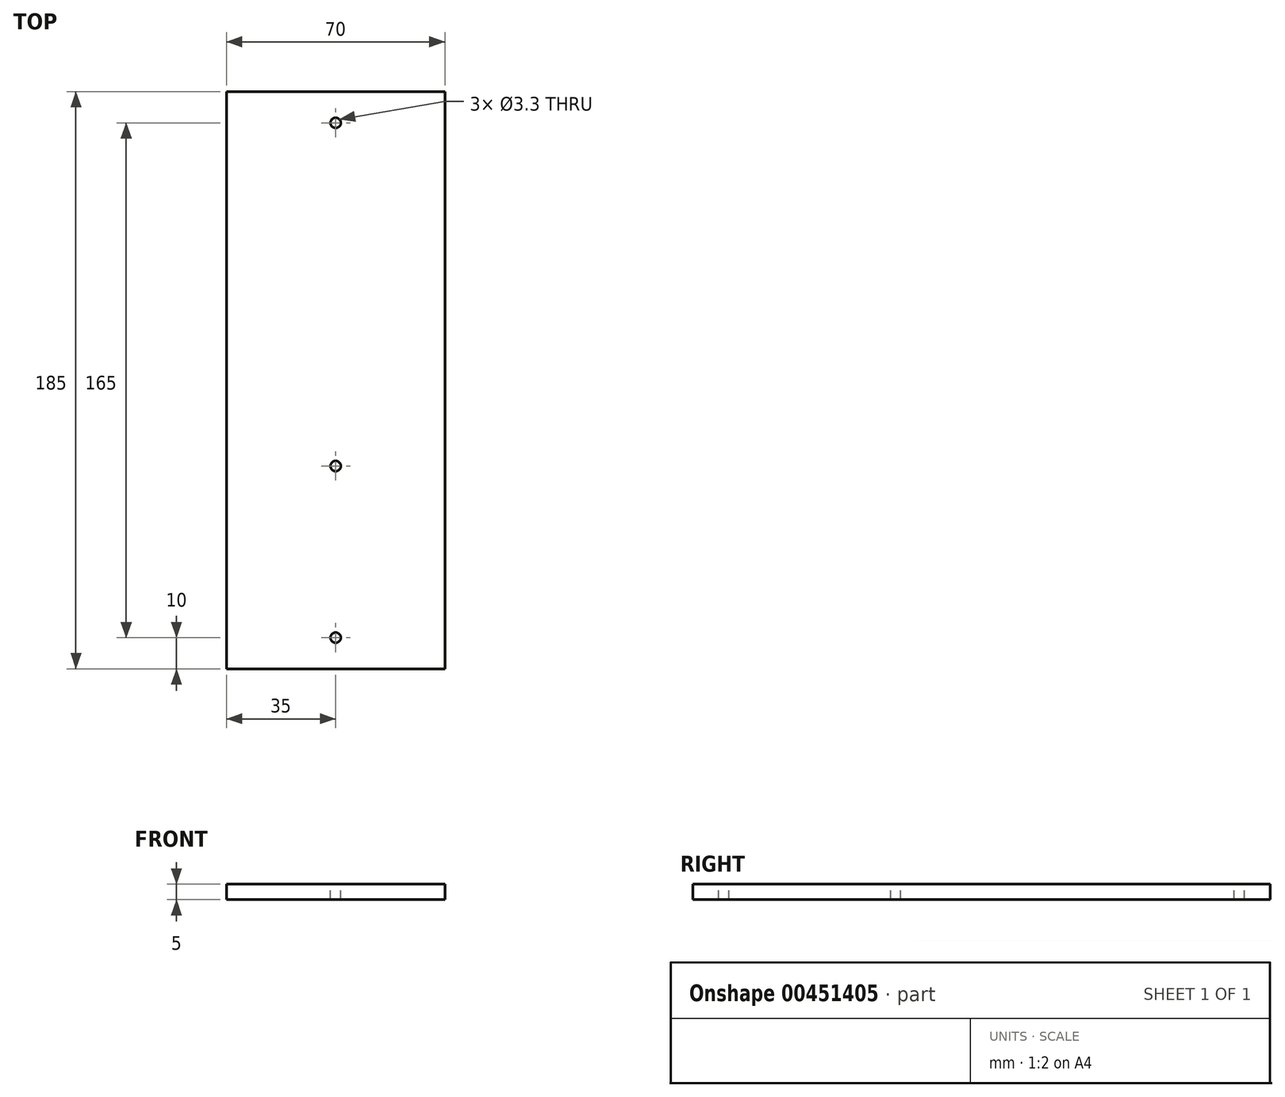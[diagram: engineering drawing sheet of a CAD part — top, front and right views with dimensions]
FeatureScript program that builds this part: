
annotation { "Feature Type Name" : "Feature", "Feature Type Description" : "" }
export const myFeature = defineFeature(function(context is Context, id is Id, definition is map)
    precondition{}
    {
        {
            var Q0;
            Q0=qCreatedBy(makeId("Top.planeOp"),FACE);
            var sketch = newSketch(context, id + "F0", { "sketchPlane" : qUnion([Q0])});
            skLineSegment(sketch, "E0.bottom", {"start": v(0, 0) * mm, "end": v(70, 0) * mm});
            skLineSegment(sketch, "E0.top", {"start": v(0, 185) * mm, "end": v(70, 185) * mm});
            skLineSegment(sketch, "E0.left", {"start": v(0, 0) * mm, "end": v(0, 185) * mm});
            skLineSegment(sketch, "E0.right", {"start": v(70, 0) * mm, "end": v(70, 185) * mm});
            skSolve(sketch);
        }
        {
            var Q0;
            Q0 = qSketchRegion(id + "F0", true);
            extrude(context, id + "F1", {"entities" : qUnion([Q0]), "depth" : 5 * mm});
        }
        {
            var Q0;
            Q0=makeQuery(id+"F1.opExtrude","CAP_FACE",FACE,{"disambiguationData":[OSD([sQuery(id+"F0.wireOp",EDGE,"E0.bottom"),sQuery(id+"F0.wireOp",EDGE,"E0.top"),sQuery(id+"F0.wireOp",EDGE,"E0.left"),sQuery(id+"F0.wireOp",EDGE,"E0.right")])],"isStart":false});
            var sketch = newSketch(context, id + "F2", { "sketchPlane" : qUnion([Q0])});
            skLineSegment(sketch, "E1", {"start": v(35, 185) * mm, "end": v(35, 0) * mm, "construction": true});
            skPoint(sketch, "E2", {"position": v(35, 10) * mm});
            skPoint(sketch, "E3", {"position": v(35, 65) * mm});
            skPoint(sketch, "E4", {"position": v(35, 175) * mm});
            skSolve(sketch);
        }
        {
            var Q0;
            Q0=sQuery(id+"F2.wireOp",VERTEX,"E4");
            var Q1;
            Q1=sQuery(id+"F2.wireOp",VERTEX,"E3");
            var Q2;
            Q2=sQuery(id+"F2.wireOp",VERTEX,"E2");
            var Q3;
            Q3=makeQuery(id+"F1.opExtrude","SWEPT_BODY",BODY,{"disambiguationData":[OSD([sQuery(id+"F0.wireOp",EDGE,"E0.bottom"),sQuery(id+"F0.wireOp",EDGE,"E0.top"),sQuery(id+"F0.wireOp",EDGE,"E0.left"),sQuery(id+"F0.wireOp",EDGE,"E0.right")])]});
            hole(context, id + "F3", {"style" : HoleStyle.SIMPLE, "endStyle" : HoleEndStyle.THROUGH, "standardTappedOrClearance" : lookupTablePath({ "standard" : "ISO", "fit" : "Normal", "size" : "M3", "type" : "Clearance" }), "standardBlindInLast" : lookupTablePath({ "fit" : "Standard", "standard" : "ISO", "size" : "M3", "type" : "Clearance" }), "holeDiameter" : 3.3 * mm, "isTappedThrough" : true, "tappedDepth" : 12 * mm, "tapClearance" : 3, "locations" : qUnion([Q0, Q1, Q2]), "scope" : qUnion([Q3])});
        }
    });
